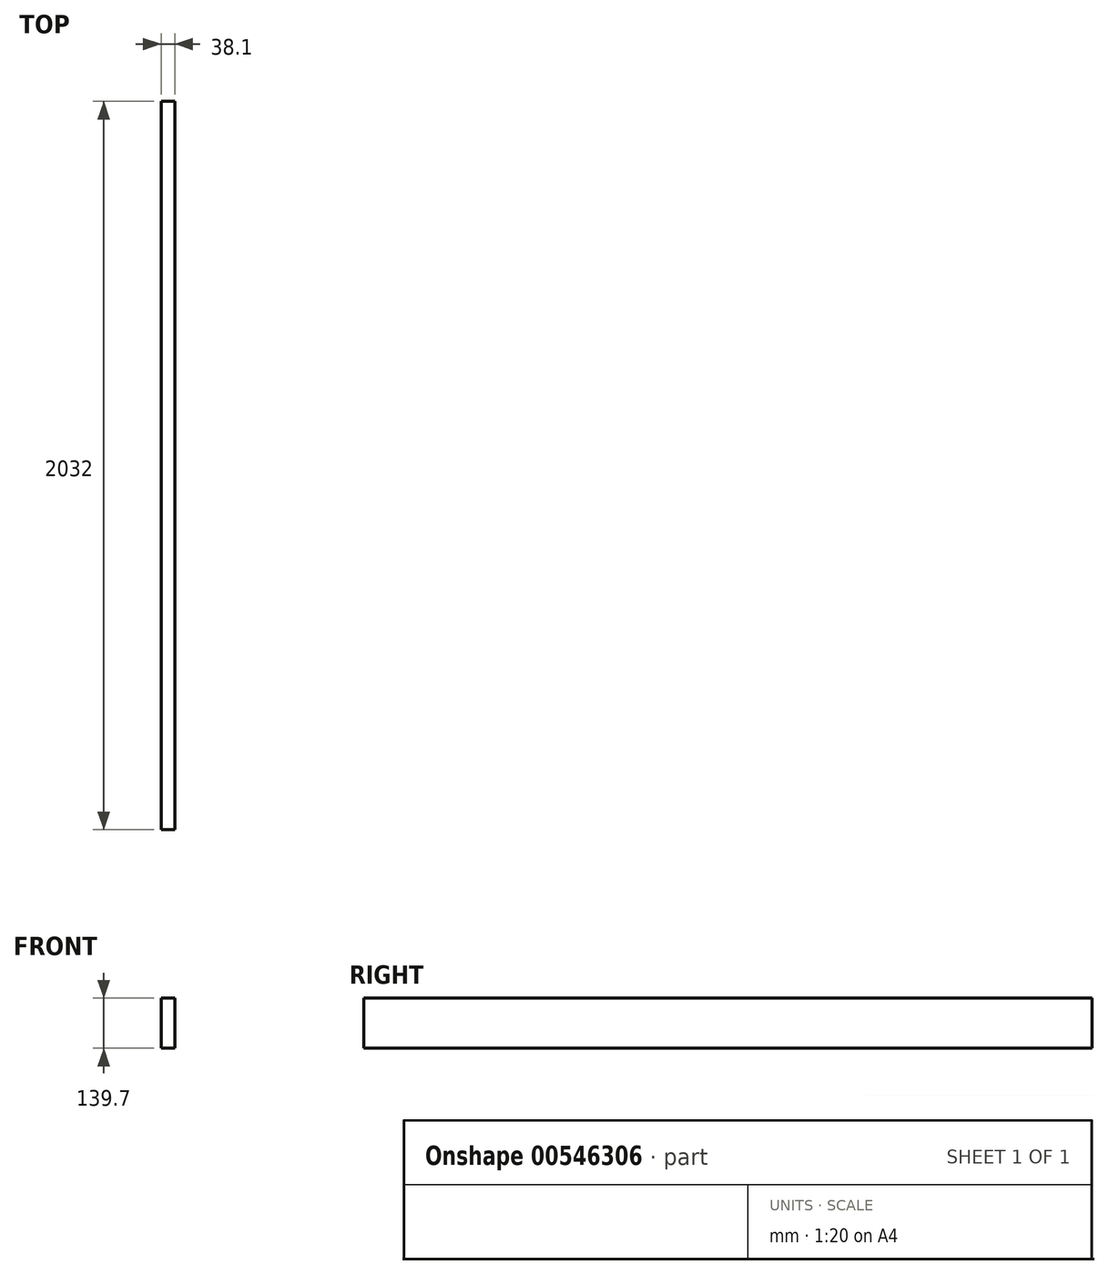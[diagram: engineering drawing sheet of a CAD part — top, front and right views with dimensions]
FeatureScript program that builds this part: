
annotation { "Feature Type Name" : "Feature", "Feature Type Description" : "" }
export const myFeature = defineFeature(function(context is Context, id is Id, definition is map)
    precondition{}
    {
        {
            var Q0;
            Q0=qCreatedBy(makeId("Front.planeOp"),FACE);
            var sketch = newSketch(context, id + "F0", { "sketchPlane" : qUnion([Q0])});
            skLineSegment(sketch, "E0", {"start": v(-176.18, -118.47) * mm, "end": v(-138.08, -118.47) * mm});
            skLineSegment(sketch, "E1", {"start": v(-138.08, -118.47) * mm, "end": v(-138.08, 21.23) * mm});
            skLineSegment(sketch, "E2", {"start": v(-138.08, 21.23) * mm, "end": v(-176.18, 21.23) * mm});
            skLineSegment(sketch, "E3", {"start": v(-176.18, 21.23) * mm, "end": v(-176.18, -118.47) * mm});
            skSolve(sketch);
        }
        {
            var Q0;
            Q0=makeQuery(id+"F0.imprint","IMPRINT",FACE,{"disambiguationData":[TD([[makeQuery(id+"F0.imprint","IMPRINT",EDGE,{"derivedFrom":sQuery(id+"F0.wireOp",EDGE,"E0")}),1.0]])]});
            extrude(context, id + "F1", {"entities" : qUnion([Q0]), "depth" : 2032 * mm, "offsetDistance" : 25.4 * mm});
        }
    });
